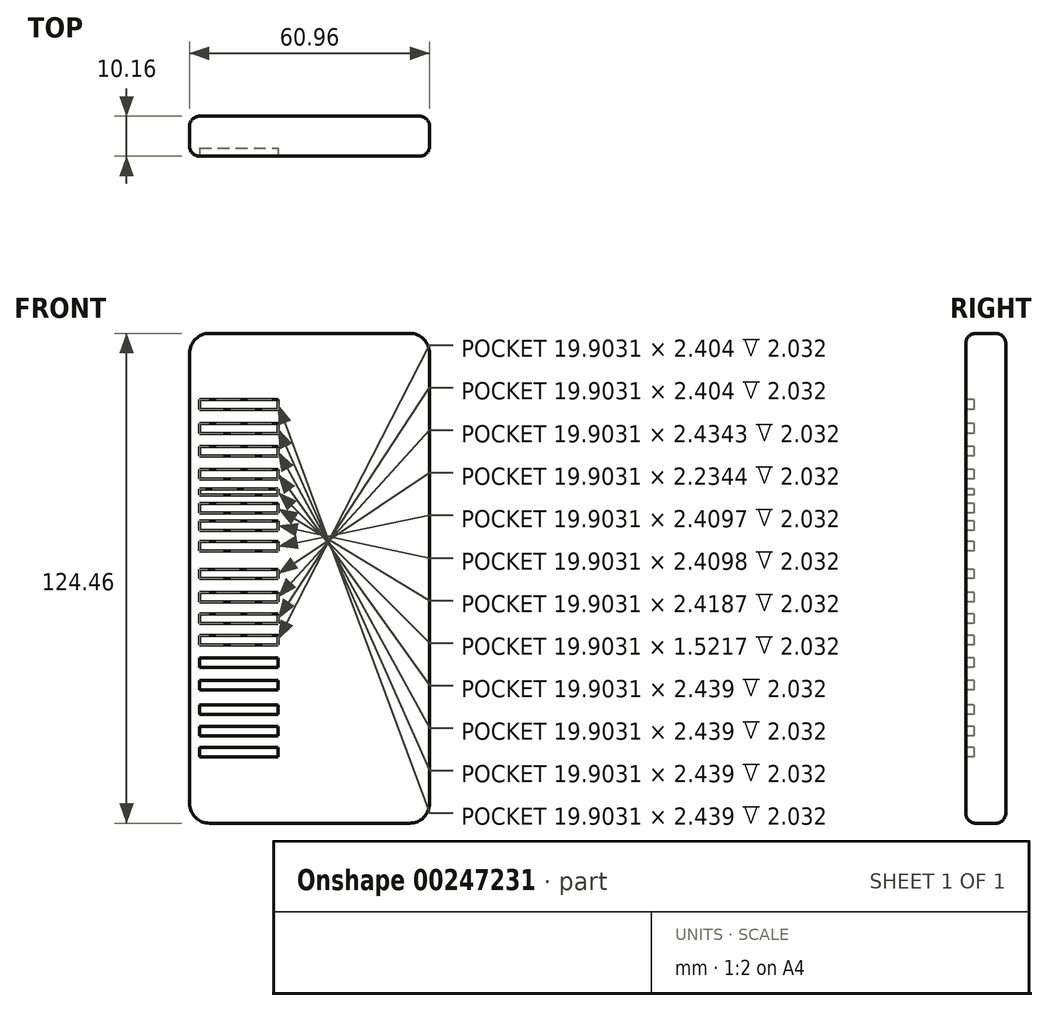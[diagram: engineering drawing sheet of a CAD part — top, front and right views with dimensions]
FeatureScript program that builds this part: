
annotation { "Feature Type Name" : "Feature", "Feature Type Description" : "" }
export const myFeature = defineFeature(function(context is Context, id is Id, definition is map)
    precondition{}
    {
        {
            var Q0;
            Q0=qCreatedBy(makeId("Front.planeOp"),FACE);
            var sketch = newSketch(context, id + "F0", { "sketchPlane" : qUnion([Q0])});
            skLineSegment(sketch, "E0.bottom", {"start": v(-44.42, 43.25) * mm, "end": v(16.54, 43.25) * mm});
            skLineSegment(sketch, "E0.top", {"start": v(-44.42, -81.2) * mm, "end": v(16.54, -81.2) * mm});
            skLineSegment(sketch, "E0.left", {"start": v(-44.42, 43.25) * mm, "end": v(-44.42, -81.2) * mm});
            skLineSegment(sketch, "E0.right", {"start": v(16.54, 43.25) * mm, "end": v(16.54, -81.2) * mm});
            skSolve(sketch);
        }
        {
            var Q0;
            Q0 = qSketchRegion(id + "F0", true);
            extrude(context, id + "F1", {"entities" : qUnion([Q0]), "endBound" : BoundingType.SYMMETRIC, "depth" : 10.16 * mm});
        }
        {
            var Q0;
            Q0=makeQuery(id+"F1.opExtrude","SWEPT_EDGE",EDGE,{"disambiguationData":[OSD([sQuery(id+"F0.wireOp",EDGE,"E0.bottom"),sQuery(id+"F0.wireOp",EDGE,"E0.right")])]});
            fillet(context, id + "F2", {"entities" : qUnion([Q0]), "radius" : 5.08 * mm, "tangentPropagation" : true, "allowEdgeOverflow" : false});
        }
        {
            var Q0;
            Q0=makeQuery(id+"F1.opExtrude","SWEPT_EDGE",EDGE,{"disambiguationData":[OSD([sQuery(id+"F0.wireOp",EDGE,"E0.bottom"),sQuery(id+"F0.wireOp",EDGE,"E0.left")])]});
            fillet(context, id + "F3", {"entities" : qUnion([Q0]), "radius" : 5.08 * mm, "tangentPropagation" : true, "allowEdgeOverflow" : false});
        }
        {
            var Q0;
            Q0=makeQuery(id+"F1.opExtrude","SWEPT_EDGE",EDGE,{"disambiguationData":[OSD([sQuery(id+"F0.wireOp",EDGE,"E0.top"),sQuery(id+"F0.wireOp",EDGE,"E0.right")])]});
            fillet(context, id + "F4", {"entities" : qUnion([Q0]), "radius" : 5.08 * mm, "tangentPropagation" : true, "allowEdgeOverflow" : false});
        }
        {
            var Q0;
            Q0=makeQuery(id+"F1.opExtrude","SWEPT_EDGE",EDGE,{"disambiguationData":[OSD([sQuery(id+"F0.wireOp",EDGE,"E0.top"),sQuery(id+"F0.wireOp",EDGE,"E0.left")])]});
            fillet(context, id + "F5", {"entities" : qUnion([Q0]), "radius" : 5.08 * mm, "tangentPropagation" : true, "allowEdgeOverflow" : false});
        }
        {
            var Q0;
            Q0=makeQuery(id+"F1.opExtrude","CAP_EDGE",EDGE,{"disambiguationData":[OSD([sQuery(id+"F0.wireOp",EDGE,"E0.right")])],"isStart":false});
            fillet(context, id + "F6", {"entities" : qUnion([Q0]), "radius" : 2.54 * mm, "tangentPropagation" : true, "allowEdgeOverflow" : false});
        }
        {
            var Q0;
            Q0=makeQuery(id+"F1.opExtrude","CAP_EDGE",EDGE,{"disambiguationData":[OSD([sQuery(id+"F0.wireOp",EDGE,"E0.right")])],"isStart":true});
            fillet(context, id + "F7", {"entities" : qUnion([Q0]), "radius" : 2.54 * mm, "tangentPropagation" : true, "allowEdgeOverflow" : false});
        }
        {
            var Q0;
            Q0=makeQuery(id+"F1.opExtrude","CAP_FACE",FACE,{"disambiguationData":[OSD([sQuery(id+"F0.wireOp",EDGE,"E0.bottom"),sQuery(id+"F0.wireOp",EDGE,"E0.top"),sQuery(id+"F0.wireOp",EDGE,"E0.left"),sQuery(id+"F0.wireOp",EDGE,"E0.right")])],"isStart":false});
            var sketch = newSketch(context, id + "F8", { "sketchPlane" : qUnion([Q0])});
            skLineSegment(sketch, "E1.bottom", {"start": v(-41.88, 26.4) * mm, "end": v(-21.98, 26.4) * mm});
            skLineSegment(sketch, "E1.top", {"start": v(-41.88, 23.95) * mm, "end": v(-21.98, 23.95) * mm});
            skLineSegment(sketch, "E1.left", {"start": v(-41.88, 26.4) * mm, "end": v(-41.88, 23.95) * mm});
            skLineSegment(sketch, "E1.right", {"start": v(-21.98, 26.4) * mm, "end": v(-21.98, 23.95) * mm});
            skLineSegment(sketch, "E2.bottom", {"start": v(-41.88, 20.3) * mm, "end": v(-21.98, 20.3) * mm});
            skLineSegment(sketch, "E2.top", {"start": v(-41.88, 17.85) * mm, "end": v(-21.98, 17.85) * mm});
            skLineSegment(sketch, "E2.left", {"start": v(-41.88, 20.3) * mm, "end": v(-41.88, 17.85) * mm});
            skLineSegment(sketch, "E2.right", {"start": v(-21.98, 20.3) * mm, "end": v(-21.98, 17.85) * mm});
            skLineSegment(sketch, "E3.bottom", {"start": v(-41.88, 14.5) * mm, "end": v(-21.98, 14.5) * mm});
            skLineSegment(sketch, "E3.top", {"start": v(-41.88, 12.06) * mm, "end": v(-21.98, 12.06) * mm});
            skLineSegment(sketch, "E3.left", {"start": v(-41.88, 14.5) * mm, "end": v(-41.88, 12.06) * mm});
            skLineSegment(sketch, "E3.right", {"start": v(-21.98, 14.5) * mm, "end": v(-21.98, 12.06) * mm});
            skLineSegment(sketch, "E4.bottom", {"start": v(-41.88, 8.7) * mm, "end": v(-21.98, 8.7) * mm});
            skLineSegment(sketch, "E4.top", {"start": v(-41.88, 6.27) * mm, "end": v(-21.98, 6.27) * mm});
            skLineSegment(sketch, "E4.left", {"start": v(-41.88, 8.7) * mm, "end": v(-41.88, 6.27) * mm});
            skLineSegment(sketch, "E4.right", {"start": v(-21.98, 8.7) * mm, "end": v(-21.98, 6.27) * mm});
            skLineSegment(sketch, "E5.bottom", {"start": v(-41.88, 3.73) * mm, "end": v(-21.98, 3.73) * mm});
            skLineSegment(sketch, "E5.top", {"start": v(-41.88, 2.2) * mm, "end": v(-21.98, 2.2) * mm});
            skLineSegment(sketch, "E5.left", {"start": v(-41.88, 3.73) * mm, "end": v(-41.88, 2.2) * mm});
            skLineSegment(sketch, "E5.right", {"start": v(-21.98, 3.73) * mm, "end": v(-21.98, 2.2) * mm});
            skPoint(sketch, "E6.firstSnap0", {"position": v(-41.88, 7.49) * mm});
            skLineSegment(sketch, "E6.bottom", {"start": v(-41.88, 0) * mm, "end": v(-21.98, 0) * mm});
            skLineSegment(sketch, "E6.top", {"start": v(-41.88, -2.42) * mm, "end": v(-21.98, -2.42) * mm});
            skLineSegment(sketch, "E6.left", {"start": v(-41.88, 0) * mm, "end": v(-41.88, -2.42) * mm});
            skLineSegment(sketch, "E6.right", {"start": v(-21.98, 0) * mm, "end": v(-21.98, -2.42) * mm});
            skLineSegment(sketch, "E7.bottom", {"start": v(-21.98, -4.4) * mm, "end": v(-41.88, -4.4) * mm});
            skLineSegment(sketch, "E7.top", {"start": v(-21.98, -6.81) * mm, "end": v(-41.88, -6.81) * mm});
            skLineSegment(sketch, "E7.left", {"start": v(-21.98, -4.4) * mm, "end": v(-21.98, -6.81) * mm});
            skLineSegment(sketch, "E7.right", {"start": v(-41.88, -4.4) * mm, "end": v(-41.88, -6.81) * mm});
            skLineSegment(sketch, "E8.bottom", {"start": v(-41.88, -9.65) * mm, "end": v(-21.98, -9.65) * mm});
            skLineSegment(sketch, "E8.top", {"start": v(-41.88, -12.06) * mm, "end": v(-21.98, -12.06) * mm});
            skLineSegment(sketch, "E8.left", {"start": v(-41.88, -9.65) * mm, "end": v(-41.88, -12.06) * mm});
            skLineSegment(sketch, "E8.right", {"start": v(-21.98, -9.65) * mm, "end": v(-21.98, -12.06) * mm});
            skPoint(sketch, "E9.oppositeSnap0", {"position": v(-41.88, -18.98) * mm});
            skLineSegment(sketch, "E9.bottom", {"start": v(-41.88, -16.74) * mm, "end": v(-21.98, -16.74) * mm});
            skLineSegment(sketch, "E9.top", {"start": v(-41.88, -18.98) * mm, "end": v(-21.98, -18.98) * mm});
            skLineSegment(sketch, "E9.left", {"start": v(-41.88, -16.74) * mm, "end": v(-41.88, -18.98) * mm});
            skLineSegment(sketch, "E9.right", {"start": v(-21.98, -16.74) * mm, "end": v(-21.98, -18.98) * mm});
            skLineSegment(sketch, "E10.bottom", {"start": v(-41.88, -22.61) * mm, "end": v(-21.98, -22.61) * mm});
            skLineSegment(sketch, "E10.top", {"start": v(-41.88, -25.05) * mm, "end": v(-21.98, -25.05) * mm});
            skLineSegment(sketch, "E10.left", {"start": v(-41.88, -22.61) * mm, "end": v(-41.88, -25.05) * mm});
            skLineSegment(sketch, "E10.right", {"start": v(-21.98, -22.61) * mm, "end": v(-21.98, -25.05) * mm});
            skLineSegment(sketch, "E11.bottom", {"start": v(-41.88, -28.05) * mm, "end": v(-21.98, -28.05) * mm});
            skLineSegment(sketch, "E11.top", {"start": v(-41.88, -30.45) * mm, "end": v(-21.98, -30.45) * mm});
            skLineSegment(sketch, "E11.left", {"start": v(-41.88, -28.05) * mm, "end": v(-41.88, -30.45) * mm});
            skLineSegment(sketch, "E11.right", {"start": v(-21.98, -28.05) * mm, "end": v(-21.98, -30.45) * mm});
            skLineSegment(sketch, "E12.bottom", {"start": v(-41.88, -33.45) * mm, "end": v(-21.98, -33.45) * mm});
            skLineSegment(sketch, "E12.top", {"start": v(-41.88, -35.86) * mm, "end": v(-21.98, -35.86) * mm});
            skLineSegment(sketch, "E12.left", {"start": v(-41.88, -33.45) * mm, "end": v(-41.88, -35.86) * mm});
            skLineSegment(sketch, "E12.right", {"start": v(-21.98, -33.45) * mm, "end": v(-21.98, -35.86) * mm});
            skLineSegment(sketch, "E13.bottom", {"start": v(-41.88, -39.16) * mm, "end": v(-21.98, -39.16) * mm});
            skLineSegment(sketch, "E13.top", {"start": v(-41.88, -41.57) * mm, "end": v(-21.98, -41.57) * mm});
            skLineSegment(sketch, "E13.left", {"start": v(-41.88, -39.16) * mm, "end": v(-41.88, -41.57) * mm});
            skLineSegment(sketch, "E13.right", {"start": v(-21.98, -39.16) * mm, "end": v(-21.98, -41.57) * mm});
            skLineSegment(sketch, "E14.bottom", {"start": v(-41.88, -44.87) * mm, "end": v(-21.98, -44.87) * mm});
            skLineSegment(sketch, "E14.top", {"start": v(-41.88, -47.28) * mm, "end": v(-21.98, -47.28) * mm});
            skLineSegment(sketch, "E14.left", {"start": v(-41.88, -44.87) * mm, "end": v(-41.88, -47.28) * mm});
            skLineSegment(sketch, "E14.right", {"start": v(-21.98, -44.87) * mm, "end": v(-21.98, -47.28) * mm});
            skLineSegment(sketch, "E15.bottom", {"start": v(-41.88, -51.18) * mm, "end": v(-21.98, -51.18) * mm});
            skLineSegment(sketch, "E15.top", {"start": v(-41.88, -53.59) * mm, "end": v(-21.98, -53.59) * mm});
            skLineSegment(sketch, "E15.left", {"start": v(-41.88, -51.18) * mm, "end": v(-41.88, -53.59) * mm});
            skLineSegment(sketch, "E15.right", {"start": v(-21.98, -51.18) * mm, "end": v(-21.98, -53.59) * mm});
            skLineSegment(sketch, "E16.bottom", {"start": v(-41.88, -56.6) * mm, "end": v(-21.98, -56.6) * mm});
            skLineSegment(sketch, "E16.top", {"start": v(-41.88, -59) * mm, "end": v(-21.98, -59) * mm});
            skLineSegment(sketch, "E16.left", {"start": v(-41.88, -56.6) * mm, "end": v(-41.88, -59) * mm});
            skLineSegment(sketch, "E16.right", {"start": v(-21.98, -56.6) * mm, "end": v(-21.98, -59) * mm});
            skLineSegment(sketch, "E17.bottom", {"start": v(-41.88, -62) * mm, "end": v(-21.98, -62) * mm});
            skLineSegment(sketch, "E17.top", {"start": v(-41.88, -64.4) * mm, "end": v(-21.98, -64.4) * mm});
            skLineSegment(sketch, "E17.left", {"start": v(-41.88, -62) * mm, "end": v(-41.88, -64.4) * mm});
            skLineSegment(sketch, "E17.right", {"start": v(-21.98, -62) * mm, "end": v(-21.98, -64.4) * mm});
            skSolve(sketch);
        }
        {
            var Q0;
            Q0 = qSketchRegion(id + "F8", true);
            extrude(context, id + "F9", {"entities" : qUnion([Q0]), "operationType" : NewBodyOperationType.REMOVE, "oppositeDirection" : true, "depth" : 2.03 * mm});
        }
    });
